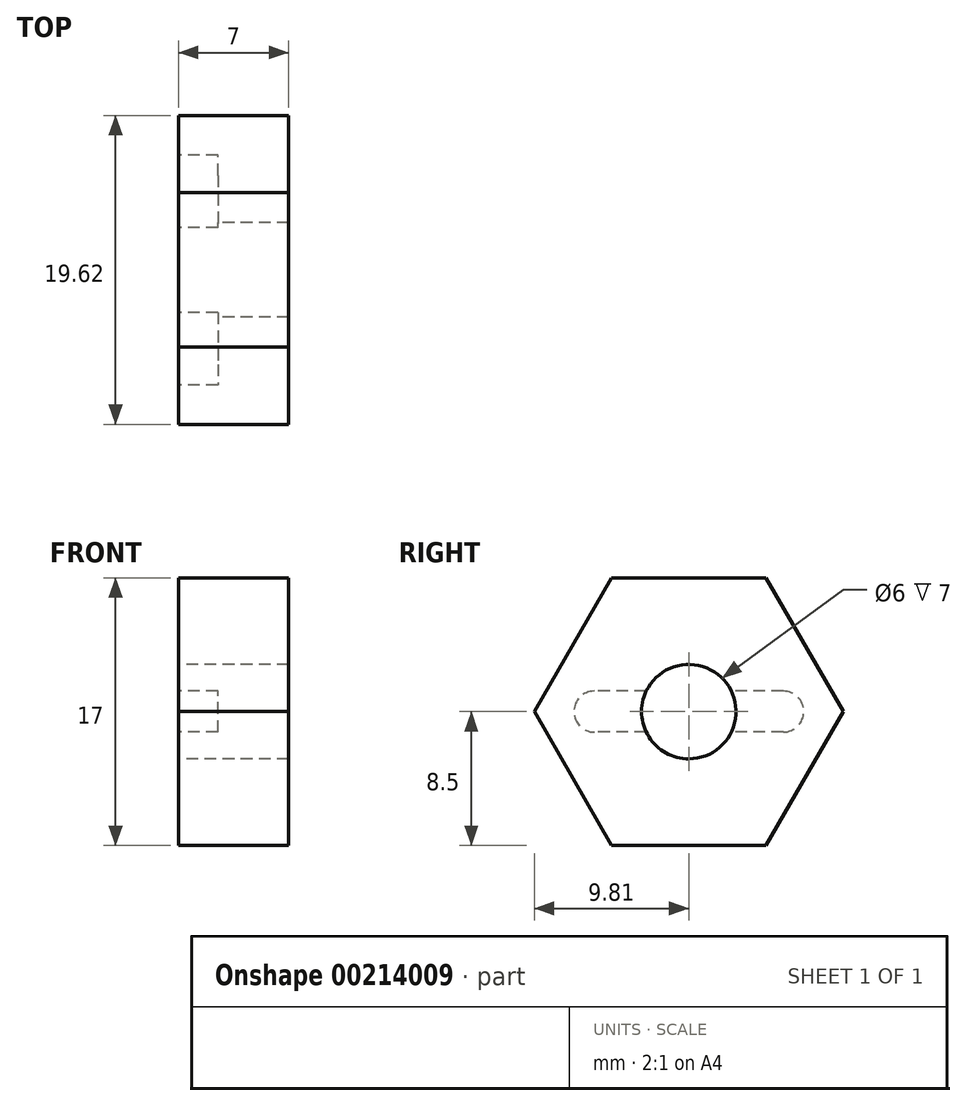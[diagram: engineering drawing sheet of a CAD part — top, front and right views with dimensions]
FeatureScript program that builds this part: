
annotation { "Feature Type Name" : "Feature", "Feature Type Description" : "" }
export const myFeature = defineFeature(function(context is Context, id is Id, definition is map)
    precondition{}
    {
        {
            var Q0;
            Q0=qCreatedBy(makeId("Right.planeOp"),FACE);
            var sketch = newSketch(context, id + "F0", { "sketchPlane" : qUnion([Q0])});
            skCircle(sketch, "E0.cCircle", {"center": v(0, 0) * mm, "radius": 8.5 * mm, "construction": true});
            skLineSegment(sketch, "E0.0", {"start": v(-4.9, 8.5) * mm, "end": v(4.9, 8.5) * mm});
            skLineSegment(sketch, "E0.1", {"start": v(4.9, 8.5) * mm, "end": v(9.81, 0) * mm});
            skLineSegment(sketch, "E0.2", {"start": v(9.81, 0) * mm, "end": v(4.9, -8.5) * mm});
            skLineSegment(sketch, "E0.3", {"start": v(4.9, -8.5) * mm, "end": v(-4.9, -8.5) * mm});
            skLineSegment(sketch, "E0.4", {"start": v(-4.9, -8.5) * mm, "end": v(-9.81, 0) * mm});
            skLineSegment(sketch, "E0.5", {"start": v(-9.81, 0) * mm, "end": v(-4.9, 8.5) * mm});
            skPoint(sketch, "E0.0.midPoint", {"position": v(0, 8.5) * mm});
            skCircle(sketch, "E1", {"center": v(0, 0) * mm, "radius": 3 * mm});
            skSolve(sketch);
        }
        {
            var Q0;
            Q0 = qSketchRegion(id + "F0", true);
            extrude(context, id + "F1", {"entities" : qUnion([Q0]), "depth" : 7 * mm});
        }
        {
            var Q0;
            Q0=makeQuery(id+"F1.opExtrude","CAP_FACE",FACE,{"disambiguationData":[OSD([sQuery(id+"F0.wireOp",EDGE,"E0.0"),sQuery(id+"F0.wireOp",EDGE,"E0.1"),sQuery(id+"F0.wireOp",EDGE,"E0.2"),sQuery(id+"F0.wireOp",EDGE,"E0.3"),sQuery(id+"F0.wireOp",EDGE,"E0.4"),sQuery(id+"F0.wireOp",EDGE,"E0.5"),sQuery(id+"F0.wireOp",EDGE,"E1")])],"isStart":true});
            var sketch = newSketch(context, id + "F2", { "sketchPlane" : qUnion([Q0])});
            skLineSegment(sketch, "E2", {"start": v(-6, 1.3) * mm, "end": v(6, 1.3) * mm});
            skLineSegment(sketch, "E3", {"start": v(-6, 0) * mm, "end": v(6, 0) * mm, "construction": true});
            skLineSegment(sketch, "E4.MirrorCS", {"start": v(-6, -1.3) * mm, "end": v(6, -1.3) * mm});
            skLineSegment(sketch, "E5", {"start": v(0, 0) * mm, "end": v(0, 1.3) * mm, "construction": true});
            skArc(sketch, "E6", {"start": v(-6, 1.3) * mm, "mid": v(-7.3, 0) * mm, "end": v(-6, -1.3) * mm});
            skArc(sketch, "E7", {"start": v(6, 1.3) * mm, "mid": v(7.3, 0) * mm, "end": v(6, -1.3) * mm});
            skSolve(sketch);
        }
        {
            var Q0;
            Q0 = qSketchRegion(id + "F2", true);
            extrude(context, id + "F3", {"entities" : qUnion([Q0]), "operationType" : NewBodyOperationType.REMOVE, "oppositeDirection" : true, "depth" : 2.5 * mm});
        }
    });
